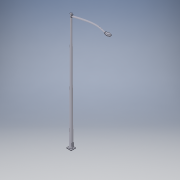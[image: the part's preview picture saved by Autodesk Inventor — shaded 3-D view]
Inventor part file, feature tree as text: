
AUTODESK INVENTOR PART (.ipt)
format: ipt  version: 2019 (Build 230136000, 136)  size: 466,944 bytes
history: native  units: in
note: dims shown in document units (in); Inventor stores cm internally (conversion verified against a paired STEP export)
features: sketch x8, extrude x4, plane x3, projected_geometry x2, revolve x1, loft x1, fillet x1
ambient origin geometry x8: Origin, YZ Plane, XZ Plane, XY Plane, X Axis, Y Axis, Z Axis, Center Point
bodies: Solid1 (feature_tree)
feature tree (20):
  revolve  "Revolution1"  [1 undecoded]
  plane  "Work Plane1"
  extrude  "Extrusion1"  Depth=2.0in
  sketch  "Sketch3"  dims[d4=0.25in d5=0.25in]
  sketch  "Sketch4"  dims[d6=2.0in d7=2.0in d8=0.3in]
  plane  "Work Plane2"
  loft  "Loft1"
  plane  "Work Plane3"
  extrude  "Extrusion2"  Depth=2.0in
  fillet  "Fillet1"  Radius=0.3in
  extrude  "Extrusion3"  Depth=1.1in
  extrude  "Extrusion4"  Depth=0.125in
  sketch  "Sketch1"  dims[d0=6.0in d1=1.0in]
  sketch  "Sketch2"  dims[d2=2.0in d3=300.0in]
  projected_geometry  "Projected Loop1"
  sketch  "Sketch5"  dims[d9=0.5in d10=1.1in]
  sketch  "Sketch6"  dims[d11=1.5in d12=0.125in]
  sketch  "Sketch7"  dims[d13=0.125in]
  sketch  "Sketch8"  dims[d14=0.6604in d15=0.9813in d16=1.8221in d17=0.0in d18=90.0deg d19=2.0in d20=5.0in d21=2.0in d22=0.5in d23=1.0in d24=0.0in d25=4.0in d26=2.5in d27=2.5in d28=84.0in d29=6.0in d30=53.0in d31=11.0in d32=10.0in d33=1.0in d34=3.0in d35=11.0in d36=87.0in d37=3.0in d38=0.0in d39=90.0deg d40=0.0in d41=90.0deg d42=0.0in d43=90.0deg d44=301.5in d45=3.0in d46=16.0in d47=6.0in d48=14.5in d49=5.0in d50=3.75in d51=4.0in d52=0.0in d53=1.5in d54=1.0in d55=0.0in d56=2.0in d57=6.0in d58=6.0in d59=5.0in d60=0.0in]
  projected_geometry  "Projected Loop2"
note: 1 required parameter value undecoded (feature->parameter linkage not recoverable at this tier; creation-order binding heuristic only, values carry confidence <= 0.55)
